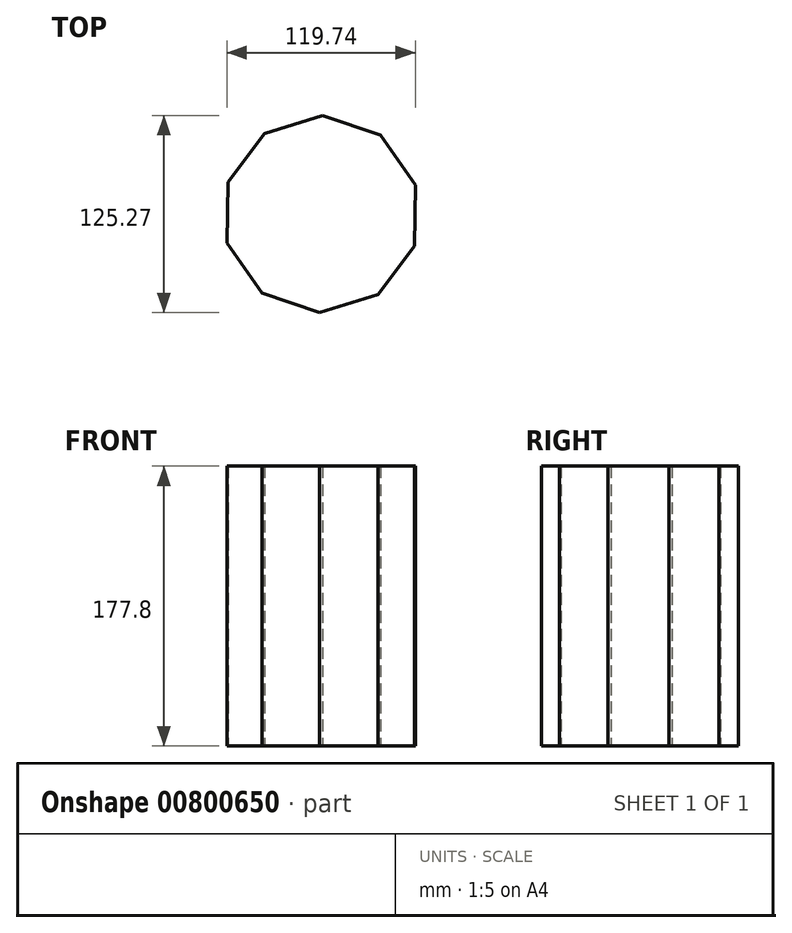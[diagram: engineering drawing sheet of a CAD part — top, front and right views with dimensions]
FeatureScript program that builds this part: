
annotation { "Feature Type Name" : "Feature", "Feature Type Description" : "" }
export const myFeature = defineFeature(function(context is Context, id is Id, definition is map)
    precondition{}
    {
        {
            var Q0;
            Q0=qCreatedBy(makeId("Top.planeOp"),FACE);
            var sketch = newSketch(context, id + "F0", { "sketchPlane" : qUnion([Q0])});
            skCircle(sketch, "E0.cCircle", {"center": v(0, 13.68) * mm, "radius": 59.57 * mm, "construction": true});
            skLineSegment(sketch, "E0.0", {"start": v(37.6, 63.77) * mm, "end": v(59.87, 32.1) * mm});
            skLineSegment(sketch, "E0.1", {"start": v(59.87, 32.1) * mm, "end": v(59.27, -6.6) * mm});
            skLineSegment(sketch, "E0.2", {"start": v(59.27, -6.6) * mm, "end": v(36.02, -37.57) * mm});
            skLineSegment(sketch, "E0.3", {"start": v(36.02, -37.57) * mm, "end": v(-0.98, -48.96) * mm});
            skLineSegment(sketch, "E0.4", {"start": v(-0.98, -48.96) * mm, "end": v(-37.6, -36.42) * mm});
            skLineSegment(sketch, "E0.5", {"start": v(-37.6, -36.42) * mm, "end": v(-59.87, -4.75) * mm});
            skLineSegment(sketch, "E0.6", {"start": v(-59.87, -4.75) * mm, "end": v(-59.27, 33.96) * mm});
            skLineSegment(sketch, "E0.7", {"start": v(-59.27, 33.96) * mm, "end": v(-36.02, 64.92) * mm});
            skLineSegment(sketch, "E0.8", {"start": v(-36.02, 64.92) * mm, "end": v(0.98, 76.3) * mm});
            skLineSegment(sketch, "E0.9", {"start": v(0.98, 76.3) * mm, "end": v(37.6, 63.77) * mm});
            skPoint(sketch, "E0.0.midPoint", {"position": v(48.74, 47.94) * mm});
            skSolve(sketch);
        }
        {
            var Q0;
            Q0=makeQuery(id+"F0.imprint","IMPRINT",FACE,{"disambiguationData":[TD([[makeQuery(id+"F0.imprint","IMPRINT",EDGE,{"derivedFrom":sQuery(id+"F0.wireOp",EDGE,"E0.0")}),-1.0]])]});
            extrude(context, id + "F1", {"entities" : qUnion([Q0]), "depth" : 177.8 * mm, "offsetDistance" : 25.4 * mm});
        }
    });
